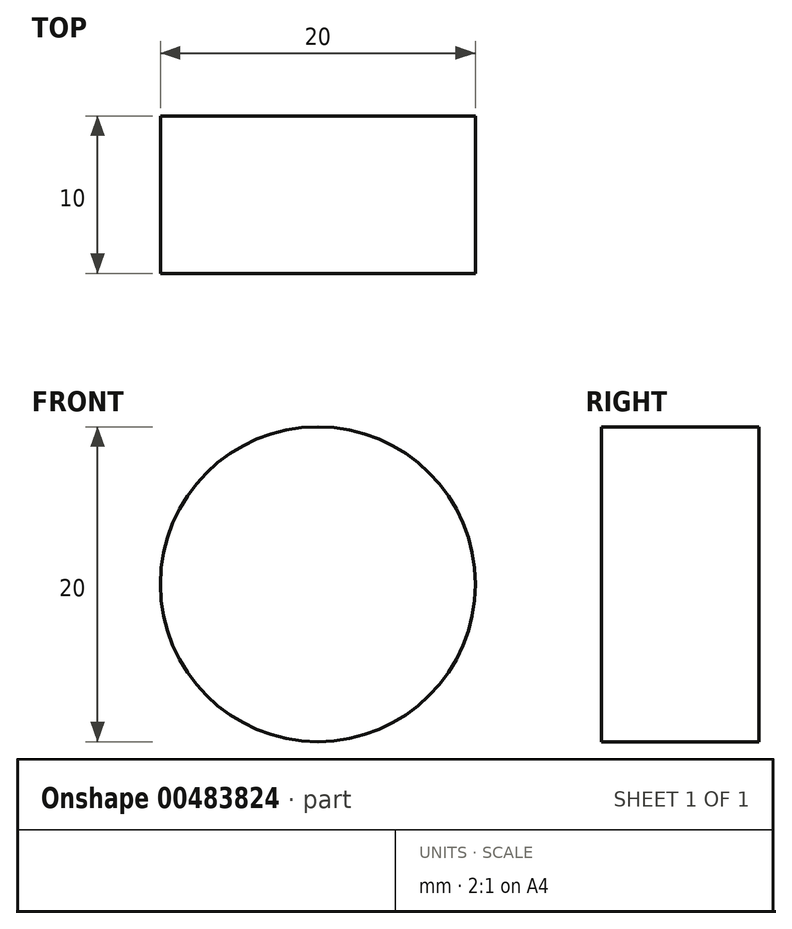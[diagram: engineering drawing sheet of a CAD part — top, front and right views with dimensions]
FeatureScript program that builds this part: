
annotation { "Feature Type Name" : "Feature", "Feature Type Description" : "" }
export const myFeature = defineFeature(function(context is Context, id is Id, definition is map)
    precondition{}
    {
        {
            var Q0;
            Q0=qCreatedBy(makeId("Front.planeOp"),FACE);
            var sketch = newSketch(context, id + "F0", { "sketchPlane" : qUnion([Q0])});
            skCircle(sketch, "E0", {"center": v(0, 0) * mm, "radius": 10 * mm});
            skSolve(sketch);
        }
        {
            var Q0;
            Q0 = qSketchRegion(id + "F0", true);
            extrude(context, id + "F1", {"entities" : qUnion([Q0]), "depth" : 10 * mm});
        }
    });
